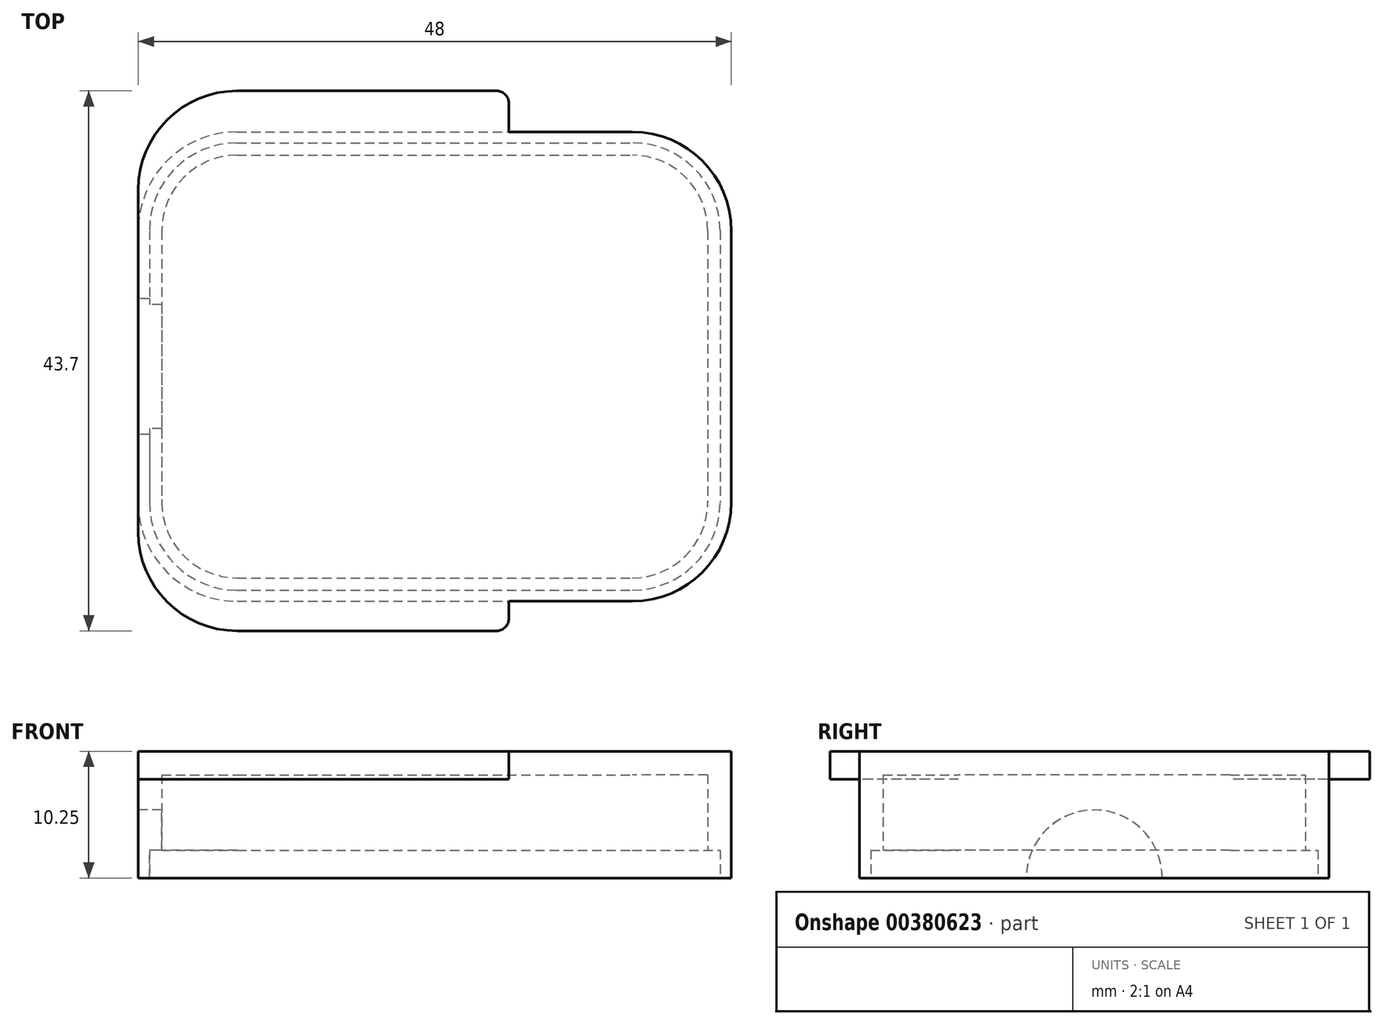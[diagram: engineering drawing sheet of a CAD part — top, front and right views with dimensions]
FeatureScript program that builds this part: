
annotation { "Feature Type Name" : "Feature", "Feature Type Description" : "" }
export const myFeature = defineFeature(function(context is Context, id is Id, definition is map)
    precondition{}
    {
        {
            var Q0;
            Q0=qCreatedBy(makeId("Top.planeOp"),FACE);
            var sketch = newSketch(context, id + "F0", { "sketchPlane" : qUnion([Q0])});
            skLineSegment(sketch, "E0.bottom", {"start": v(-16, 19) * mm, "end": v(16, 19) * mm});
            skLineSegment(sketch, "E0.top", {"start": v(-16, -19) * mm, "end": v(16, -19) * mm});
            skLineSegment(sketch, "E0.left", {"start": v(-24, 11) * mm, "end": v(-24, -11) * mm});
            skLineSegment(sketch, "E0.right", {"start": v(24, 11) * mm, "end": v(24, -11) * mm});
            skPoint(sketch, "E1.visualSharp", {"position": v(-24, 19) * mm});
            skArc(sketch, "E1.filletArc", {"start": v(-16, 19) * mm, "mid": v(-21.66, 16.66) * mm, "end": v(-24, 11) * mm});
            skPoint(sketch, "E2.visualSharp", {"position": v(-24, -19) * mm});
            skArc(sketch, "E2.filletArc", {"start": v(-24, -11) * mm, "mid": v(-21.66, -16.66) * mm, "end": v(-16, -19) * mm});
            skPoint(sketch, "E3.visualSharp", {"position": v(24, -19) * mm});
            skArc(sketch, "E3.filletArc", {"start": v(16, -19) * mm, "mid": v(21.66, -16.66) * mm, "end": v(24, -11) * mm});
            skPoint(sketch, "E4.visualSharp", {"position": v(24, 19) * mm});
            skArc(sketch, "E4.filletArc", {"start": v(24, 11) * mm, "mid": v(21.66, 16.66) * mm, "end": v(16, 19) * mm});
            skSolve(sketch);
        }
        {
            var Q0;
            Q0=makeQuery(id+"F0.imprint","IMPRINT",FACE,{"disambiguationData":[TD([[makeQuery(id+"F0.imprint","IMPRINT",EDGE,{"derivedFrom":sQuery(id+"F0.wireOp",EDGE,"E0.bottom")}),-1.0]])]});
            extrude(context, id + "F1", {"entities" : qUnion([Q0]), "depth" : 10.25 * mm});
        }
        {
            var Q0;
            Q0=makeQuery(id+"F1.opExtrude","CAP_FACE",FACE,{"disambiguationData":[OSD([sQuery(id+"F0.wireOp",EDGE,"E0.bottom"),sQuery(id+"F0.wireOp",EDGE,"E0.top"),sQuery(id+"F0.wireOp",EDGE,"E0.left"),sQuery(id+"F0.wireOp",EDGE,"E0.right"),sQuery(id+"F0.wireOp",EDGE,"E1.filletArc"),sQuery(id+"F0.wireOp",EDGE,"E2.filletArc"),sQuery(id+"F0.wireOp",EDGE,"E3.filletArc"),sQuery(id+"F0.wireOp",EDGE,"E4.filletArc")])],"isStart":false});
            var sketch = newSketch(context, id + "F2", { "sketchPlane" : qUnion([Q0])});
            skLineSegment(sketch, "E5.bottom", {"start": v(-16, 22.3) * mm, "end": v(6, 22.3) * mm});
            skLineSegment(sketch, "E5.top", {"start": v(-16, -21.4) * mm, "end": v(6, -21.4) * mm});
            skLineSegment(sketch, "E5.left", {"start": v(-24, 14.3) * mm, "end": v(-24, -13.4) * mm});
            skLineSegment(sketch, "E5.right", {"start": v(6, 22.3) * mm, "end": v(6, -21.4) * mm});
            skPoint(sketch, "E6.visualSharp", {"position": v(-24, -21.4) * mm});
            skArc(sketch, "E6.filletArc", {"start": v(-24, -13.4) * mm, "mid": v(-21.66, -19.05) * mm, "end": v(-16, -21.4) * mm});
            skPoint(sketch, "E7.visualSharp", {"position": v(-24, 22.3) * mm});
            skArc(sketch, "E7.filletArc", {"start": v(-16, 22.3) * mm, "mid": v(-21.66, 19.97) * mm, "end": v(-24, 14.3) * mm});
            skSolve(sketch);
        }
        {
            var Q0;
            {var subQ4=sQuery(id+"F2.wireOp",EDGE,"E5.bottom");Q0=makeQuery(id+"F2.imprint","IMPRINT",FACE,{"disambiguationData":[TD([[makeQuery(id+"F2.imprint","IMPRINT",EDGE,{"derivedFrom":subQ4}),-1.0]])]});}
            var Q1;
            {var subQ2=sQuery(id+"F2.wireOp",EDGE,"E5.top");Q1=makeQuery(id+"F2.imprint","IMPRINT",FACE,{"disambiguationData":[TD([[makeQuery(id+"F2.imprint","IMPRINT",EDGE,{"derivedFrom":subQ2}),1.0]])]});}
            extrude(context, id + "F3", {"entities" : qUnion([Q0, Q1]), "operationType" : NewBodyOperationType.ADD, "oppositeDirection" : true, "depth" : 2.25 * mm});
        }
        {
            var Q0;
            Q0=makeQuery(id+"F3.opExtrude","SWEPT_EDGE",EDGE,{"disambiguationData":[OSD([sQuery(id+"F2.wireOp",EDGE,"E5.top"),sQuery(id+"F2.wireOp",EDGE,"E5.right")])]});
            var Q1;
            Q1=makeQuery(id+"F3.opExtrude","SWEPT_EDGE",EDGE,{"disambiguationData":[OSD([sQuery(id+"F0.wireOp",EDGE,"E0.top"),sQuery(id+"F2.wireOp",EDGE,"E5.right")])]});
            var Q2;
            Q2=makeQuery(id+"F3.opExtrude","SWEPT_EDGE",EDGE,{"disambiguationData":[OSD([sQuery(id+"F0.wireOp",EDGE,"E0.bottom"),sQuery(id+"F2.wireOp",EDGE,"E5.right")])]});
            var Q3;
            Q3=makeQuery(id+"F3.opExtrude","SWEPT_EDGE",EDGE,{"disambiguationData":[OSD([sQuery(id+"F2.wireOp",EDGE,"E5.bottom"),sQuery(id+"F2.wireOp",EDGE,"E5.right")])]});
            fillet(context, id + "F4", {"entities" : qUnion([Q0, Q1, Q2, Q3]), "radius" : 1 * mm, "tangentPropagation" : true, "allowEdgeOverflow" : false});
        }
        {
            var Q0;
            Q0=makeQuery(id+"F1.opExtrude","CAP_FACE",FACE,{"disambiguationData":[OSD([sQuery(id+"F0.wireOp",EDGE,"E0.bottom"),sQuery(id+"F0.wireOp",EDGE,"E0.top"),sQuery(id+"F0.wireOp",EDGE,"E0.left"),sQuery(id+"F0.wireOp",EDGE,"E0.right"),sQuery(id+"F0.wireOp",EDGE,"E1.filletArc"),sQuery(id+"F0.wireOp",EDGE,"E2.filletArc"),sQuery(id+"F0.wireOp",EDGE,"E3.filletArc"),sQuery(id+"F0.wireOp",EDGE,"E4.filletArc")])],"isStart":true});
            shell(context, id + "F5", {"entities" : qUnion([Q0]), "thickness" : 1.9 * mm});
        }
        {
            var Q0;
            Q0=makeQuery(id+"F1.opExtrude","CAP_FACE",FACE,{"disambiguationData":[OSD([sQuery(id+"F0.wireOp",EDGE,"E0.bottom"),sQuery(id+"F0.wireOp",EDGE,"E0.top"),sQuery(id+"F0.wireOp",EDGE,"E0.left"),sQuery(id+"F0.wireOp",EDGE,"E0.right"),sQuery(id+"F0.wireOp",EDGE,"E1.filletArc"),sQuery(id+"F0.wireOp",EDGE,"E2.filletArc"),sQuery(id+"F0.wireOp",EDGE,"E3.filletArc"),sQuery(id+"F0.wireOp",EDGE,"E4.filletArc")])],"isStart":true});
            var sketch = newSketch(context, id + "F6", { "sketchPlane" : qUnion([Q0])});
            skArc(sketch, "E8.0", {"start": v(-16, -17.1) * mm, "mid": v(-20.31, -15.31) * mm, "end": v(-22.1, -11) * mm});
            skLineSegment(sketch, "E9.0", {"start": v(-22.1, -11) * mm, "end": v(-22.1, 11) * mm});
            skArc(sketch, "E10.0", {"start": v(-22.1, 11) * mm, "mid": v(-20.31, 15.31) * mm, "end": v(-16, 17.1) * mm});
            skLineSegment(sketch, "E11.0", {"start": v(-16, 17.1) * mm, "end": v(16, 17.1) * mm});
            skArc(sketch, "E12.0", {"start": v(16, 17.1) * mm, "mid": v(20.31, 15.31) * mm, "end": v(22.1, 11) * mm});
            skLineSegment(sketch, "E13.0", {"start": v(22.1, -11) * mm, "end": v(22.1, 11) * mm});
            skArc(sketch, "E14.0", {"start": v(22.1, -11) * mm, "mid": v(20.31, -15.31) * mm, "end": v(16, -17.1) * mm});
            skLineSegment(sketch, "E15.0", {"start": v(-16, -17.1) * mm, "end": v(16, -17.1) * mm});
            skArc(sketch, "E16.0", {"start": v(-23.1, 11) * mm, "mid": v(-21.02, 16.02) * mm, "end": v(-16, 18.1) * mm});
            skLineSegment(sketch, "E16.1", {"start": v(-23.1, -11) * mm, "end": v(-23.1, 11) * mm});
            skLineSegment(sketch, "E16.2", {"start": v(-16, 18.1) * mm, "end": v(16, 18.1) * mm});
            skArc(sketch, "E16.3", {"start": v(-16, -18.1) * mm, "mid": v(-21.02, -16.02) * mm, "end": v(-23.1, -11) * mm});
            skArc(sketch, "E16.4", {"start": v(16, 18.1) * mm, "mid": v(21.02, 16.02) * mm, "end": v(23.1, 11) * mm});
            skLineSegment(sketch, "E16.5", {"start": v(23.1, -11) * mm, "end": v(23.1, 11) * mm});
            skArc(sketch, "E16.6", {"start": v(23.1, -11) * mm, "mid": v(21.02, -16.02) * mm, "end": v(16, -18.1) * mm});
            skLineSegment(sketch, "E16.7", {"start": v(-16, -18.1) * mm, "end": v(16, -18.1) * mm});
            skSolve(sketch);
        }
        {
            var Q0;
            Q0=makeQuery(id+"F6.imprint","IMPRINT",FACE,{"disambiguationData":[TD([[makeQuery(id+"F6.imprint","IMPRINT",EDGE,{"derivedFrom":sQuery(id+"F6.wireOp",EDGE,"E8.0")}),1.0]])]});
            extrude(context, id + "F7", {"entities" : qUnion([Q0]), "operationType" : NewBodyOperationType.REMOVE, "oppositeDirection" : true, "depth" : 2.25 * mm});
        }
        {
            var Q0;
            {var subQ0=sQuery(id+"F2.wireOp",EDGE,"E5.left");Q0=makeQuery(id+"F3.boolean.opBoolean","MERGE",FACE,{"derivedFrom":[makeQuery(id+"F1.opExtrude","SWEPT_FACE",FACE,{"disambiguationData":[OSD([sQuery(id+"F0.wireOp",EDGE,"E0.left")])]}),makeQuery(id+"F3.opExtrude","SWEPT_FACE",FACE,{"disambiguationData":[OSD([subQ0]),TDD([makeQuery(id+"F2.imprint","IMPRINT",EDGE,{"disambiguationData":[TD([[makeQuery(id+"F2.imprint","INTERSECT",VERTEX,{"derivedFrom":[makeQuery(id+"F1.opExtrude","CAP_EDGE",EDGE,{"disambiguationData":[OSD([sQuery(id+"F0.wireOp",EDGE,"E1.filletArc")])],"isStart":false}),subQ0]}),1.0]])],"derivedFrom":subQ0})])]}),makeQuery(id+"F3.opExtrude","SWEPT_FACE",FACE,{"disambiguationData":[OSD([subQ0]),TDD([makeQuery(id+"F2.imprint","IMPRINT",EDGE,{"disambiguationData":[TD([[makeQuery(id+"F2.imprint","INTERSECT",VERTEX,{"derivedFrom":[makeQuery(id+"F1.opExtrude","CAP_EDGE",EDGE,{"disambiguationData":[OSD([sQuery(id+"F0.wireOp",EDGE,"E2.filletArc")])],"isStart":false}),subQ0]}),-1.0]])],"derivedFrom":subQ0})])]})]});}
            var sketch = newSketch(context, id + "F8", { "sketchPlane" : qUnion([Q0])});
            skArc(sketch, "E17", {"start": v(5.5, 0) * mm, "mid": v(0, 5.5) * mm, "end": v(-5.5, 0) * mm});
            skSolve(sketch);
        }
        {
            var Q0;
            {var subQ0=sQuery(id+"F8.wireOp",EDGE,"E17");Q0=makeQuery(id+"F8.imprint","IMPRINT",FACE,{"disambiguationData":[TD([[makeQuery(id+"F8.imprint","IMPRINT",EDGE,{"derivedFrom":subQ0}),1.0]])]});}
            extrude(context, id + "F9", {"entities" : qUnion([Q0]), "operationType" : NewBodyOperationType.REMOVE, "oppositeDirection" : true, "depth" : 6.4 * mm});
        }
    });
